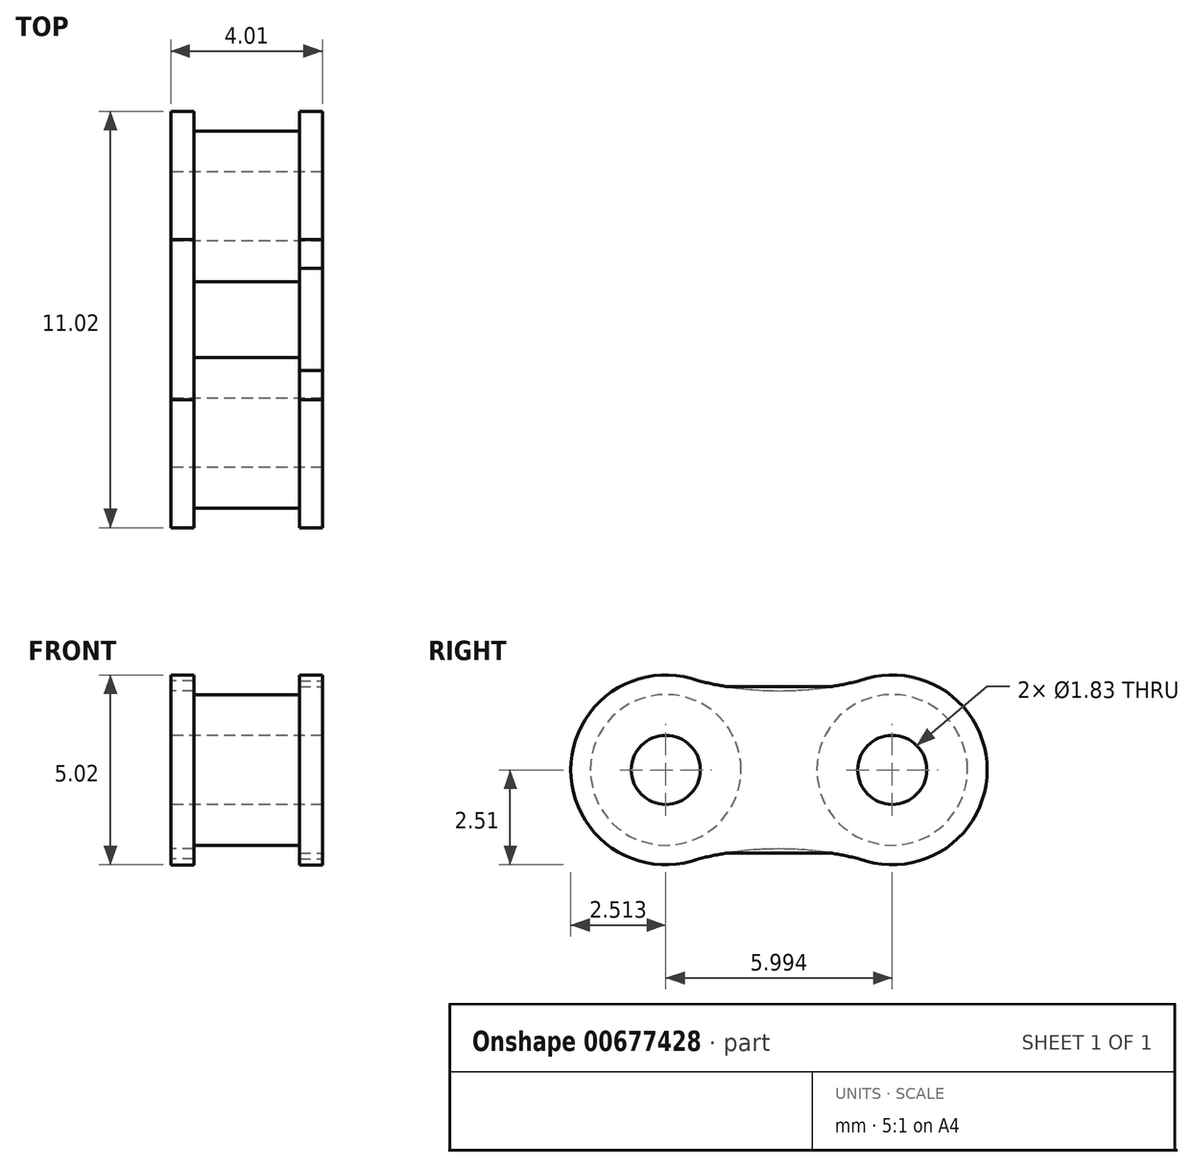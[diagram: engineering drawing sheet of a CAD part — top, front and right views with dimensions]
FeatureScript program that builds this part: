
annotation { "Feature Type Name" : "Feature", "Feature Type Description" : "" }
export const myFeature = defineFeature(function(context is Context, id is Id, definition is map)
    precondition{}
    {
        {
            var Q0;
            Q0=qCreatedBy(makeId("Right.planeOp"),FACE);
            var sketch = newSketch(context, id + "F0", { "sketchPlane" : qUnion([Q0])});
            skArc(sketch, "E0", {"start": v(-2.12, 2.36) * mm, "mid": v(-5.51, 0) * mm, "end": v(-2.12, -2.36) * mm});
            skArc(sketch, "E1", {"start": v(2.12, -2.36) * mm, "mid": v(5.51, 0) * mm, "end": v(2.12, 2.36) * mm});
            skArc(sketch, "E2", {"start": v(-2.12, 2.36) * mm, "mid": v(0, 2.1) * mm, "end": v(2.12, 2.36) * mm});
            skArc(sketch, "E3.MirrorCS", {"start": v(-2.12, -2.36) * mm, "mid": v(0, -2.1) * mm, "end": v(2.12, -2.36) * mm});
            skCircle(sketch, "E4", {"center": v(-3, 0) * mm, "radius": 0.91 * mm});
            skCircle(sketch, "E5.MirrorC", {"center": v(3, 0) * mm, "radius": 0.91 * mm});
            skSolve(sketch);
        }
        {
            var Q0;
            Q0 = qSketchRegion(id + "F0", true);
            extrude(context, id + "F1", {"entities" : qUnion([Q0]), "endBound" : BoundingType.SYMMETRIC, "depth" : 0.6 * mm, "offsetDistance" : 25 * mm});
        }
        {
            var Q0;
            Q0=makeQuery(id+"F1.opExtrude","CAP_FACE",FACE,{"disambiguationData":[OSD([sQuery(id+"F0.wireOp",EDGE,"E0"),sQuery(id+"F0.wireOp",EDGE,"E1"),sQuery(id+"F0.wireOp",EDGE,"E2"),sQuery(id+"F0.wireOp",EDGE,"E3.MirrorCS"),sQuery(id+"F0.wireOp",EDGE,"E4"),sQuery(id+"F0.wireOp",EDGE,"E5.MirrorC")])],"isStart":false});
            var sketch = newSketch(context, id + "F2", { "sketchPlane" : qUnion([Q0])});
            skCircle(sketch, "E6", {"center": v(-3, 0) * mm, "radius": 0.91 * mm});
            skCircle(sketch, "E7", {"center": v(-3, 0) * mm, "radius": 2 * mm});
            skSolve(sketch);
        }
        {
            var Q0;
            Q0 = qSketchRegion(id + "F2", true);
            extrude(context, id + "F3", {"entities" : qUnion([Q0]), "operationType" : NewBodyOperationType.ADD, "depth" : 2.8 * mm / 2, "offsetDistance" : 25 * mm});
        }
        {
            var Q0;
            Q0=makeQuery(id+"F1.opExtrude","SWEPT_BODY",BODY,{"disambiguationData":[OSD([sQuery(id+"F0.wireOp",EDGE,"E0"),sQuery(id+"F0.wireOp",EDGE,"E1"),sQuery(id+"F0.wireOp",EDGE,"E2"),sQuery(id+"F0.wireOp",EDGE,"E3.MirrorCS"),sQuery(id+"F0.wireOp",EDGE,"E4"),sQuery(id+"F0.wireOp",EDGE,"E5.MirrorC")])]});
            var Q1;
            Q1=qCreatedBy(makeId("Front.planeOp"),FACE);
            mirror(context, id + "F4", {"operationType" : NewBodyOperationType.ADD, "entities" : qUnion([Q0]), "mirrorPlane" : qUnion([Q1])});
        }
        {
            var Q0;
            Q0=makeQuery(id+"F1.opExtrude","SWEPT_BODY",BODY,{"disambiguationData":[OSD([sQuery(id+"F0.wireOp",EDGE,"E0"),sQuery(id+"F0.wireOp",EDGE,"E1"),sQuery(id+"F0.wireOp",EDGE,"E2"),sQuery(id+"F0.wireOp",EDGE,"E3.MirrorCS"),sQuery(id+"F0.wireOp",EDGE,"E4"),sQuery(id+"F0.wireOp",EDGE,"E5.MirrorC")])]});
            var Q1;
            Q1=makeQuery(id+"F3.opExtrude","CAP_FACE",FACE,{"disambiguationData":[OSD([sQuery(id+"F2.wireOp",EDGE,"E6"),sQuery(id+"F2.wireOp",EDGE,"E7")])],"isStart":false});
            mirror(context, id + "F5", {"operationType" : NewBodyOperationType.ADD, "entities" : qUnion([Q0]), "mirrorPlane" : qUnion([Q1])});
        }
        {
            var Q0;
            Q0=makeQuery(id+"F5.opPattern","COPY",FACE,{"derivedFrom":makeQuery(id+"F1.opExtrude","CAP_FACE",FACE,{"disambiguationData":[OSD([sQuery(id+"F0.wireOp",EDGE,"E0"),sQuery(id+"F0.wireOp",EDGE,"E1"),sQuery(id+"F0.wireOp",EDGE,"E2"),sQuery(id+"F0.wireOp",EDGE,"E3.MirrorCS"),sQuery(id+"F0.wireOp",EDGE,"E4"),sQuery(id+"F0.wireOp",EDGE,"E5.MirrorC")])],"isStart":true}),"instanceName":"1"});
            var sketch = newSketch(context, id + "F6", { "sketchPlane" : qUnion([Q0])});
            skLineSegment(sketch, "E8", {"start": v(0, 0) * mm, "end": v(4.83, 0) * mm});
            skSolve(sketch);
        }
        {
            var Q0;
            Q0=makeQuery(id+"F6.imprint","IMPRINT",FACE,{"disambiguationData":[TD([[makeQuery(id+"F6.imprint","IMPRINT",EDGE,{"derivedFrom":makeQuery(id+"F5.opPattern","COPY",EDGE,{"derivedFrom":makeQuery(id+"F1.opExtrude","CAP_EDGE",EDGE,{"disambiguationData":[OSD([sQuery(id+"F0.wireOp",EDGE,"E0")])],"isStart":true}),"instanceName":"1"})}),1.0]])]});
            var sketch = newSketch(context, id + "F7", { "sketchPlane" : qUnion([Q0])});
            skLineSegment(sketch, "E9", {"start": v(-1.66, 2.2) * mm, "end": v(1.7, 2.2) * mm});
            skLineSegment(sketch, "E10", {"start": v(-1.66, 2.2) * mm, "end": v(0, 0) * mm});
            skLineSegment(sketch, "E11", {"start": v(0, 0) * mm, "end": v(1.7, 2.2) * mm});
            skLineSegment(sketch, "E12", {"start": v(0, 0) * mm, "end": v(-0.57, 0) * mm});
            skLineSegment(sketch, "E13.MirrorCS", {"start": v(-1.66, -2.2) * mm, "end": v(0, 0) * mm});
            skLineSegment(sketch, "E14.MirrorCS", {"start": v(-1.66, -2.2) * mm, "end": v(1.7, -2.2) * mm});
            skLineSegment(sketch, "E15.MirrorCS", {"start": v(0, 0) * mm, "end": v(1.7, -2.2) * mm});
            skSolve(sketch);
        }
        {
            var Q0;
            {var subQ0=sQuery(id+"F7.wireOp",EDGE,"E9");var subQ1=makeQuery(id+"F6.imprint","IMPRINT",EDGE,{"derivedFrom":makeQuery(id+"F5.opPattern","COPY",EDGE,{"derivedFrom":makeQuery(id+"F1.opExtrude","CAP_EDGE",EDGE,{"disambiguationData":[OSD([sQuery(id+"F0.wireOp",EDGE,"E2")])],"isStart":true}),"instanceName":"1"})});var subQ2=makeQuery(id+"F7.imprint","INTERSECT",VERTEX,{"disambiguationData":[OD(0.0)],"derivedFrom":[subQ1,subQ0]});Q0=makeQuery(id+"F7.imprint","IMPRINT",FACE,{"disambiguationData":[TD([[makeQuery(id+"F7.imprint","IMPRINT",EDGE,{"disambiguationData":[TD([[subQ2,-1.0]])],"derivedFrom":subQ0}),-1.0]])]});}
            var Q1;
            {var subQ0=sQuery(id+"F7.wireOp",EDGE,"E14.MirrorCS");var subQ1=makeQuery(id+"F6.imprint","IMPRINT",EDGE,{"derivedFrom":makeQuery(id+"F5.opPattern","COPY",EDGE,{"derivedFrom":makeQuery(id+"F1.opExtrude","CAP_EDGE",EDGE,{"disambiguationData":[OSD([sQuery(id+"F0.wireOp",EDGE,"E3.MirrorCS")])],"isStart":true}),"instanceName":"1"})});var subQ2=makeQuery(id+"F7.imprint","INTERSECT",VERTEX,{"disambiguationData":[OD(0.0)],"derivedFrom":[subQ1,subQ0]});Q1=makeQuery(id+"F7.imprint","IMPRINT",FACE,{"disambiguationData":[TD([[makeQuery(id+"F7.imprint","IMPRINT",EDGE,{"disambiguationData":[TD([[subQ2,-1.0]])],"derivedFrom":subQ0}),1.0]])]});}
            var Q2;
            Q2=makeQuery(id+"F5.opPattern","COPY",FACE,{"derivedFrom":makeQuery(id+"F1.opExtrude","CAP_FACE",FACE,{"disambiguationData":[OSD([sQuery(id+"F0.wireOp",EDGE,"E0"),sQuery(id+"F0.wireOp",EDGE,"E1"),sQuery(id+"F0.wireOp",EDGE,"E2"),sQuery(id+"F0.wireOp",EDGE,"E3.MirrorCS"),sQuery(id+"F0.wireOp",EDGE,"E4"),sQuery(id+"F0.wireOp",EDGE,"E5.MirrorC")])],"isStart":false}),"instanceName":"1"});
            extrude(context, id + "F8", {"entities" : qUnion([Q0, Q1]), "operationType" : NewBodyOperationType.ADD, "endBound" : BoundingType.UP_TO_SURFACE, "oppositeDirection" : true, "depth" : 25 * mm, "endBoundEntityFace" : qUnion([Q2]), "offsetDistance" : 25 * mm});
        }
    });
